# Revit family: 201_TINO-S-_-_-_-_
name_source: partatom
category: Air Terminals
units: mm (PartAtom-declared; Revit-internal decimal feet)

## family parameters
Always vertical = Yes
Cut with Voids When Loaded = No
Part Type = Normal
Room Calculation Point = Yes
Round Connector Dimension = Use Diameter
Shared = No
Work Plane-Based = No

## types (28) — shared parameters
CL_Location_5000 = 5000 mm  [stored 16.4042 ft]
Description = Wall diffuser
L_ARR = 400 mm  [stored 1.31234 ft]
Manufacturer = Climecon
URL = www.climecon.fi
W_ARR = 400 mm  [stored 1.31234 ft]
XRefLineVPlnId = 7453
YRefLineVPlnId = 7456
magiPartTypeId = 201
magiProductFamilyId = TINO-S-*-*-*-*
zero-valued in all types: CLBTZ, H_ARR, MC_Default_elevation

## per-type parameters (varying)
| type | B | BH2 | BH3 | H | L | L2 | S | S1 |
| TINO-S-255-150-155-100 | 155 mm | 75 mm  [stored 0.246063 ft] | 45 mm  [stored 0.147638 ft] | 100 mm | 255 mm  [stored 0.836614 ft] | 128 mm | 42 mm  [stored 0.137795 ft] | 11 mm |
| TINO-S-800-250-700-200 | 700 mm | 125 mm  [stored 0.410105 ft] | 75 mm  [stored 0.246063 ft] | 200 mm | 800 mm  [stored 2.62467 ft] | 400 mm  [stored 1.31234 ft] | 77 mm  [stored 0.252625 ft] | 19 mm |
| TINO-S-800-210-700-150 | 700 mm | 105 mm  [stored 0.344488 ft] | 63 mm | 150 mm | 800 mm  [stored 2.62467 ft] | 400 mm  [stored 1.31234 ft] | 62 mm  [stored 0.203412 ft] | 16 mm |
| TINO-S-800-175-700-125 | 700 mm | 88 mm | 53 mm | 125 mm | 800 mm  [stored 2.62467 ft] | 400 mm  [stored 1.31234 ft] | 50 mm  [stored 0.164042 ft] | 13 mm |
| TINO-S-800-150-700-100 | 700 mm | 75 mm  [stored 0.246063 ft] | 45 mm  [stored 0.147638 ft] | 100 mm | 800 mm  [stored 2.62467 ft] | 400 mm  [stored 1.31234 ft] | 42 mm  [stored 0.137795 ft] | 11 mm |
| TINO-S-700-250-600-200 | 600 mm | 125 mm  [stored 0.410105 ft] | 75 mm  [stored 0.246063 ft] | 200 mm | 700 mm  [stored 2.29659 ft] | 350 mm  [stored 1.14829 ft] | 77 mm  [stored 0.252625 ft] | 19 mm |
| TINO-S-700-210-600-150 | 600 mm | 105 mm  [stored 0.344488 ft] | 63 mm | 150 mm | 700 mm  [stored 2.29659 ft] | 350 mm  [stored 1.14829 ft] | 62 mm  [stored 0.203412 ft] | 16 mm |
| TINO-S-700-175-600-125 | 600 mm | 88 mm | 53 mm | 125 mm | 700 mm  [stored 2.29659 ft] | 350 mm  [stored 1.14829 ft] | 50 mm  [stored 0.164042 ft] | 13 mm |
| TINO-S-700-150-600-100 | 600 mm | 75 mm  [stored 0.246063 ft] | 45 mm  [stored 0.147638 ft] | 100 mm | 700 mm  [stored 2.29659 ft] | 350 mm  [stored 1.14829 ft] | 42 mm  [stored 0.137795 ft] | 11 mm |
| TINO-S-600-250-500-200 | 500 mm | 125 mm  [stored 0.410105 ft] | 75 mm  [stored 0.246063 ft] | 200 mm | 600 mm  [stored 1.9685 ft] | 300 mm  [stored 0.984252 ft] | 77 mm  [stored 0.252625 ft] | 19 mm |
| TINO-S-600-210-500-150 | 500 mm | 105 mm  [stored 0.344488 ft] | 63 mm | 150 mm | 600 mm  [stored 1.9685 ft] | 300 mm  [stored 0.984252 ft] | 62 mm  [stored 0.203412 ft] | 16 mm |
| TINO-S-600-175-500-125 | 500 mm | 88 mm | 53 mm | 125 mm | 600 mm  [stored 1.9685 ft] | 300 mm  [stored 0.984252 ft] | 50 mm  [stored 0.164042 ft] | 13 mm |
| TINO-S-600-150-500-100 | 500 mm | 75 mm  [stored 0.246063 ft] | 45 mm  [stored 0.147638 ft] | 100 mm | 600 mm  [stored 1.9685 ft] | 300 mm  [stored 0.984252 ft] | 42 mm  [stored 0.137795 ft] | 11 mm |
| TINO-S-500-250-400-200 | 400 mm | 125 mm  [stored 0.410105 ft] | 75 mm  [stored 0.246063 ft] | 200 mm | 500 mm  [stored 1.64042 ft] | 250 mm  [stored 0.82021 ft] | 77 mm  [stored 0.252625 ft] | 19 mm |
| TINO-S-500-210-400-150 | 400 mm | 105 mm  [stored 0.344488 ft] | 63 mm | 150 mm | 500 mm  [stored 1.64042 ft] | 250 mm  [stored 0.82021 ft] | 62 mm  [stored 0.203412 ft] | 16 mm |
| TINO-S-500-175-400-125 | 400 mm | 88 mm | 53 mm | 125 mm | 500 mm  [stored 1.64042 ft] | 250 mm  [stored 0.82021 ft] | 50 mm  [stored 0.164042 ft] | 13 mm |
| TINO-S-500-150-400-100 | 400 mm | 75 mm  [stored 0.246063 ft] | 45 mm  [stored 0.147638 ft] | 100 mm | 500 mm  [stored 1.64042 ft] | 250 mm  [stored 0.82021 ft] | 42 mm  [stored 0.137795 ft] | 11 mm |
| TINO-S-400-250-300-200 | 300 mm | 125 mm  [stored 0.410105 ft] | 75 mm  [stored 0.246063 ft] | 200 mm | 400 mm  [stored 1.31234 ft] | 200 mm  [stored 0.656168 ft] | 77 mm  [stored 0.252625 ft] | 19 mm |
| TINO-S-400-210-300-150 | 300 mm | 105 mm  [stored 0.344488 ft] | 63 mm | 150 mm | 400 mm  [stored 1.31234 ft] | 200 mm  [stored 0.656168 ft] | 62 mm  [stored 0.203412 ft] | 16 mm |
| TINO-S-400-175-300-125 | 300 mm | 88 mm | 53 mm | 125 mm | 400 mm  [stored 1.31234 ft] | 200 mm  [stored 0.656168 ft] | 50 mm  [stored 0.164042 ft] | 13 mm |
| TINO-S-400-150-300-100 | 300 mm | 75 mm  [stored 0.246063 ft] | 45 mm  [stored 0.147638 ft] | 100 mm | 400 mm  [stored 1.31234 ft] | 200 mm  [stored 0.656168 ft] | 42 mm  [stored 0.137795 ft] | 11 mm |
| TINO-S-300-250-200-200 | 200 mm | 125 mm  [stored 0.410105 ft] | 75 mm  [stored 0.246063 ft] | 200 mm | 300 mm  [stored 0.984252 ft] | 150 mm  [stored 0.492126 ft] | 77 mm  [stored 0.252625 ft] | 19 mm |
| TINO-S-300-210-200-150 | 200 mm | 105 mm  [stored 0.344488 ft] | 63 mm | 150 mm | 300 mm  [stored 0.984252 ft] | 150 mm  [stored 0.492126 ft] | 62 mm  [stored 0.203412 ft] | 16 mm |
| TINO-S-300-175-200-125 | 200 mm | 88 mm | 53 mm | 125 mm | 300 mm  [stored 0.984252 ft] | 150 mm  [stored 0.492126 ft] | 50 mm  [stored 0.164042 ft] | 13 mm |
| TINO-S-300-150-200-100 | 200 mm | 75 mm  [stored 0.246063 ft] | 45 mm  [stored 0.147638 ft] | 100 mm | 300 mm  [stored 0.984252 ft] | 150 mm  [stored 0.492126 ft] | 42 mm  [stored 0.137795 ft] | 11 mm |
| TINO-S-255-250-155-200 | 155 mm | 125 mm  [stored 0.410105 ft] | 75 mm  [stored 0.246063 ft] | 200 mm | 255 mm  [stored 0.836614 ft] | 128 mm | 77 mm  [stored 0.252625 ft] | 19 mm |
| TINO-S-255-210-155-150 | 155 mm | 105 mm  [stored 0.344488 ft] | 63 mm | 150 mm | 255 mm  [stored 0.836614 ft] | 128 mm | 62 mm  [stored 0.203412 ft] | 16 mm |
| TINO-S-255-175-155-125 | 155 mm | 88 mm | 53 mm | 125 mm | 255 mm  [stored 0.836614 ft] | 128 mm | 50 mm  [stored 0.164042 ft] | 13 mm |

note: column(s) folded — value = type name in every type: magiProductCode, magiProductId

note: [stored X ft] marks values corroborated as IEEE doubles in the binary element streams (Revit-internal decimal feet)

## geometry (parser evidence)
native form markers: Sweep x1
no freeform markers — native parametric forms only
